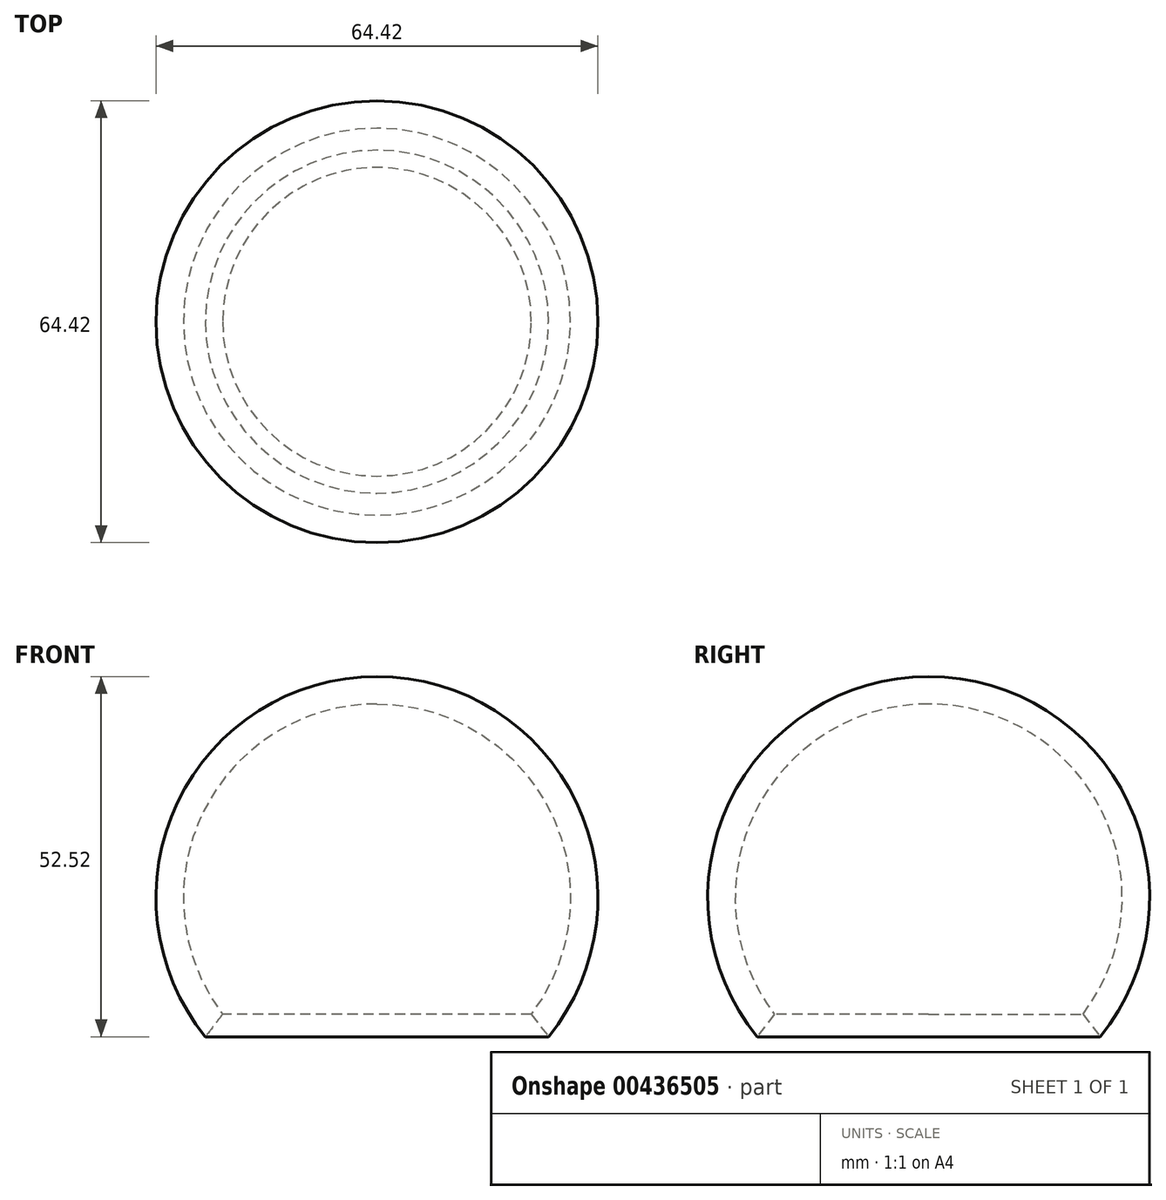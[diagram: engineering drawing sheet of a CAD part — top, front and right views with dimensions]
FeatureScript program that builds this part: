
annotation { "Feature Type Name" : "Feature", "Feature Type Description" : "" }
export const myFeature = defineFeature(function(context is Context, id is Id, definition is map)
    precondition{}
    {
        {
            var Q0;
            Q0=qCreatedBy(makeId("Front.planeOp"),FACE);
            var sketch = newSketch(context, id + "F0", { "sketchPlane" : qUnion([Q0])});
            skArc(sketch, "E0", {"start": v(22.5, 0) * mm, "mid": v(0, 45.23) * mm, "end": v(-22.5, 0) * mm});
            skArc(sketch, "E1.0", {"start": v(25, -3.3) * mm, "mid": v(0, 49.23) * mm, "end": v(-25, -3.3) * mm});
            skLineSegment(sketch, "E2", {"start": v(-25, -3.3) * mm, "end": v(-22.5, 0) * mm});
            skLineSegment(sketch, "E3", {"start": v(22.5, 0) * mm, "end": v(25, -3.3) * mm});
            skLineSegment(sketch, "E4", {"start": v(0, 0) * mm, "end": v(0, 49.23) * mm});
            skSolve(sketch);
        }
        {
            var Q0;
            {var subQ0=sQuery(id+"F0.wireOp",EDGE,"E3");Q0=makeQuery(id+"F0.imprint","IMPRINT",FACE,{"disambiguationData":[TD([[makeQuery(id+"F0.imprint","IMPRINT",EDGE,{"derivedFrom":subQ0}),1.0]])]});}
            var Q1;
            Q1=sQuery(id+"F0.wireOp",EDGE,"E4");
            revolve(context, id + "F1", {"entities" : qUnion([Q0]), "axis" : qUnion([Q1]), "revolveType" : RevolveType.FULL});
        }
    });
